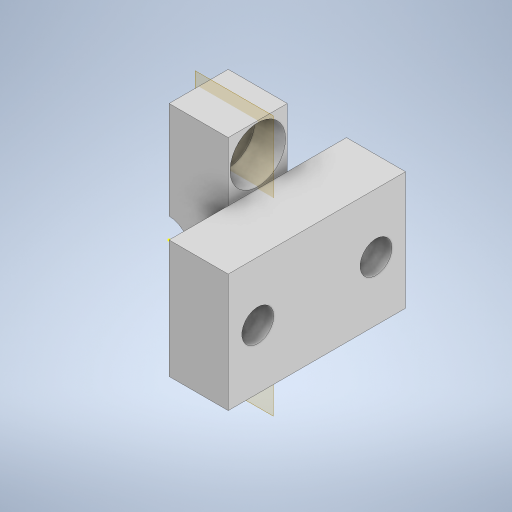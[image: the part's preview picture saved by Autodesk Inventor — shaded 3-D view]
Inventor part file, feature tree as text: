
AUTODESK INVENTOR PART (.ipt)
format: ipt  version: 2023 (Build 270158000, 158)  size: 347,648 bytes
history: native  units: mm
features: sketch x10, extrude x9, plane x1
ambient origin geometry x8: Origin, YZ Plane, XZ Plane, XY Plane, X Axis, Y Axis, Z Axis, Center Point
bodies: Solid1 (feature_tree)
feature tree (20):
  extrude  "Extrusion1"  Depth=20.0mm
  plane  "Work Plane1"
  extrude  "Extrusion2"  Depth=5.0mm
  extrude  "Extrusion3"  Depth=1.8mm
  extrude  "Extrusion4"  Depth=2.5mm
  extrude  "Extrusion5"  Depth=2.5mm
  sketch  "Sketch6"  dims[d21=2.5mm d22=2.7mm]
  extrude  "Extrusion6"  Depth=2.5mm
  extrude  "Extrusion7"  Depth=25.0mm TaperAngle=0.0deg
  extrude  "Extrusion8"  Depth=4.0mm
  extrude  "Extrusion9"  Depth=5.0mm
  sketch  "Sketch1"  dims[d0=20.0mm d1=20.0mm]
  sketch  "Sketch2"  dims[d10=5.0mm d11=0.0mm d12=5.0mm]
  sketch  "Sketch3"  dims[d13=1.8mm d14=0.0mm d15=3.5mm]
  sketch  "Sketch4"  dims[d16=8.0mm d17=0.0mm d18=2.5mm]
  sketch  "Sketch5"  dims[d19=2.5mm d20=2.5mm]
  sketch  "Sketch7"  dims[d23=2.7mm d24=25.0mm d25=0.0mm]
  sketch  "Sketch8"  dims[d26=4.0mm d27=4.0mm]
  sketch  "Sketch9"  dims[d28=4.0mm d29=0.0mm d30=5.0mm]
  sketch  "Sketch10"  dims[d31=5.0mm d32=5.0mm d33=5.0mm d34=10.0mm d35=0.0mm d36=5.0mm d37=5.0mm d38=5.0mm d39=2.7mm d40=2.7mm d41=5.0mm d42=5.0mm d43=5.0mm d44=5.0mm d45=2.5mm d46=2.5mm d47=5.0mm d48=0.0mm d49=4.0mm d50=4.0mm d51=2.0mm d52=0.0mm d53=4.7mm d54=4.7mm d55=2.6mm d56=0.0mm]
